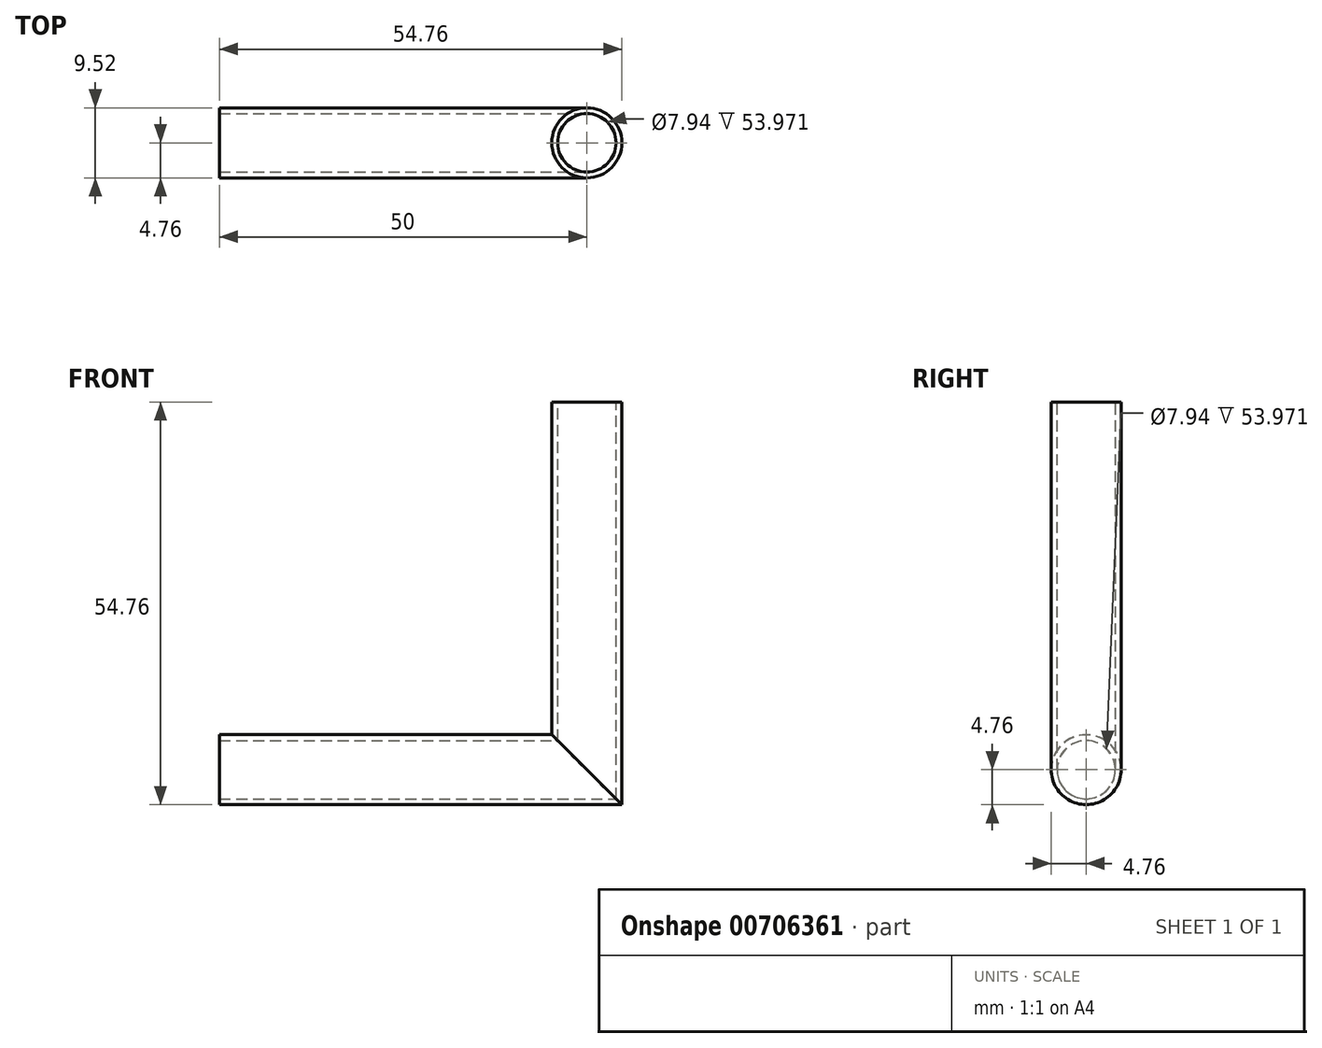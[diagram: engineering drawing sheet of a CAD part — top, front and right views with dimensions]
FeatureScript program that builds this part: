
annotation { "Feature Type Name" : "Feature", "Feature Type Description" : "" }
export const myFeature = defineFeature(function(context is Context, id is Id, definition is map)
    precondition{}
    {
        {
            var Q0;
            Q0=qCreatedBy(makeId("Right.planeOp"),FACE);
            var sketch = newSketch(context, id + "F0", { "sketchPlane" : qUnion([Q0])});
            skCircle(sketch, "E0", {"center": v(0, 0) * mm, "radius": 4.76 * mm});
            skSolve(sketch);
        }
        {
            var Q0;
            Q0=qCreatedBy(makeId("Right.planeOp"),FACE);
            var sketch = newSketch(context, id + "F1", { "sketchPlane" : qUnion([Q0])});
            skCircle(sketch, "E1", {"center": v(0, 0) * mm, "radius": 3.97 * mm});
            skSolve(sketch);
        }
        {
            var Q0;
            Q0=qCreatedBy(makeId("Front.planeOp"),FACE);
            var sketch = newSketch(context, id + "F2", { "sketchPlane" : qUnion([Q0])});
            skLineSegment(sketch, "E2", {"start": v(0, 0) * mm, "end": v(50, 0) * mm});
            skLineSegment(sketch, "E3", {"start": v(50, 0) * mm, "end": v(50, 50) * mm});
            skSolve(sketch);
        }
        {
            var Q0;
            Q0=makeQuery(id+"F0.imprint","IMPRINT",FACE,{"disambiguationData":[TD([[makeQuery(id+"F0.imprint","IMPRINT",EDGE,{"derivedFrom":sQuery(id+"F0.wireOp",EDGE,"E0")}),1.0]])]});
            var Q1;
            Q1=qConstructionFilter(qBodyType(qCreatedBy(id+"F2",EDGE),BodyType.WIRE),ConstructionObject.NO);
            sweep(context, id + "F3", {"profiles" : qUnion([Q0]), "path" : qUnion([Q1])});
        }
        {
            var Q0;
            Q0=makeQuery(id+"F1.imprint","IMPRINT",FACE,{"disambiguationData":[TD([[makeQuery(id+"F1.imprint","IMPRINT",EDGE,{"derivedFrom":sQuery(id+"F1.wireOp",EDGE,"E1")}),1.0]])]});
            var Q1;
            Q1=qConstructionFilter(qBodyType(qCreatedBy(id+"F2",EDGE),BodyType.WIRE),ConstructionObject.NO);
            sweep(context, id + "F4", {"operationType" : NewBodyOperationType.REMOVE, "profiles" : qUnion([Q0]), "path" : qUnion([Q1])});
        }
    });
